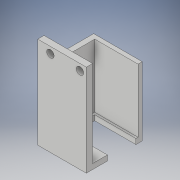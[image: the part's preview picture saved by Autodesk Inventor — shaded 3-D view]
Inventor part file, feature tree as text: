
AUTODESK INVENTOR PART (.ipt)
format: ipt  version: 2019 (Build 230136000, 136)  size: 160,768 bytes
history: native  units: mm
features: extrude x7, sketch x7, projected_geometry x1
ambient origin geometry x8: Origin, YZ Plane, XZ Plane, XY Plane, X Axis, Y Axis, Z Axis, Center Point
bodies: Solid1 (feature_tree)
feature tree (15):
  extrude  "Extrusion1"  Depth=43.5mm
  extrude  "Extrusion5"  Depth=2.5mm
  extrude  "Extrusion6"  Depth=23.5mm TaperAngle=0.0deg
  extrude  "Extrusion7"  Depth=20.5mm TaperAngle=0.0deg
  extrude  "Extrusion9"  Depth=1.0mm
  extrude  "Extrusion10"  Depth=2.5mm TaperAngle=0.0deg
  extrude  "Extrusion11"  Depth=2.5mm
  sketch  "Sketch1"  dims[d0=23.0mm d1=43.5mm]
  sketch  "Sketch6"  dims[d2=3.0mm d3=0.0mm d17=2.5mm]
  sketch  "Sketch7"  dims[d18=32.5mm d19=23.5mm d20=0.0mm]
  sketch  "Sketch8"  dims[d21=2.0mm d22=20.5mm d23=0.0mm]
  projected_geometry  "Projected Loop3"
  sketch  "Sketch10"  dims[d24=7.0mm d25=1.0mm]
  sketch  "Sketch11"  dims[d26=5.0mm d27=2.5mm d28=0.0mm]
  sketch  "Sketch12"  dims[d35=10.0mm d36=4.5mm d37=4.0mm d38=2.5mm d39=0.0mm d40=3.5mm d41=3.5mm d42=14.0mm d44=3.0mm d45=40.5mm d46=3.0mm d47=0.0mm d48=4.0mm d49=6.0mm d50=2.5mm d51=0.0mm]
